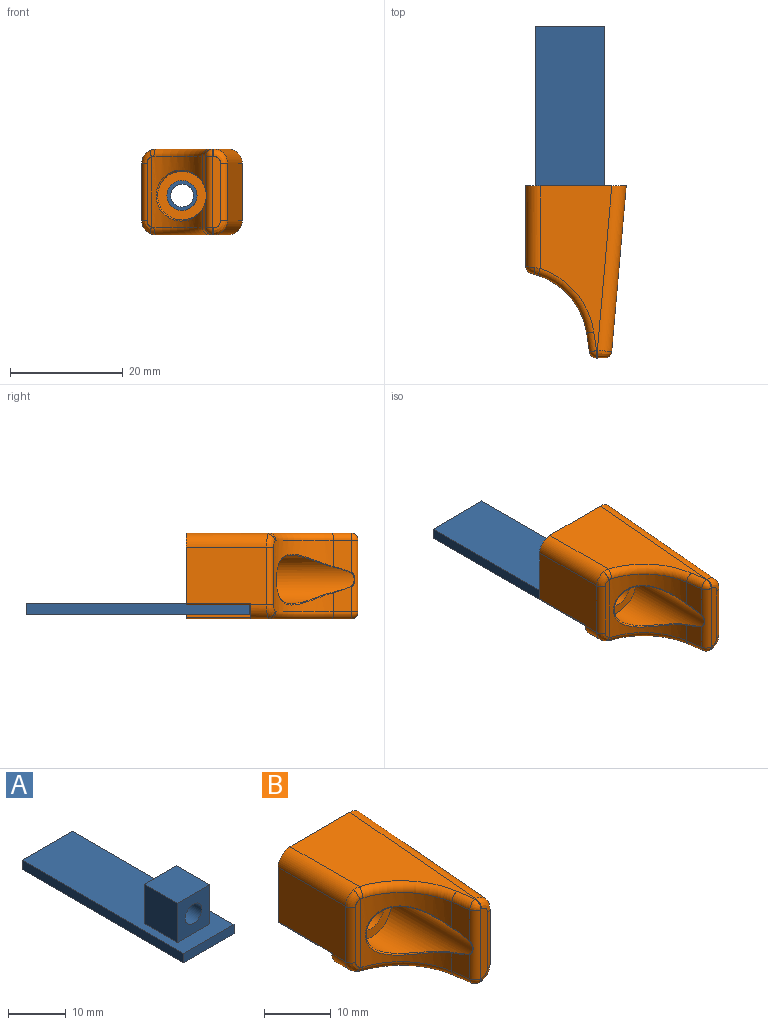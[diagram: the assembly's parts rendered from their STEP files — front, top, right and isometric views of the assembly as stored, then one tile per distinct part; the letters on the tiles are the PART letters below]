
ASSEMBLY  parts=2 mates=1
PART A: 12 faces, bbox 12.3x39.6x10.3 mm
  f0: plane 39.62x12.27mm, normal (0,0,1), area 421.8mm2, adj f1,f2,f3,f4,f6,f7,f8,f9
  f1: plane 39.62x1.96mm, normal (-1,0,0), area 77.5mm2, adj f0,f2,f4,f5
  f2: plane 12.27x1.96mm, normal (0,-1,0), area 24mm2, adj f0,f1,f3,f5
  f3: plane 39.62x1.96mm, normal (1,0,0), area 77.5mm2, adj f0,f2,f4,f5
  f4: plane 12.27x1.96mm, normal (0,1,0), area 24mm2, adj f0,f1,f3,f5
  f5: plane 39.62x12.27mm, normal (0,0,-1), area 486mm2, adj f1,f2,f3,f4
  f6: plane 8.31x8.13mm, normal (-1,0,0), area 67.5mm2, adj f0,f7,f9,f10
  f7: plane 8.31x7.9mm, normal (0,-1,0), area 52.6mm2, adj f0,f6,f8,f10,f11
  f8: plane 8.31x8.13mm, normal (1,0,0), area 67.5mm2, adj f0,f7,f9,f10
  f9: plane 8.31x7.9mm, normal (0,1,0), area 52.6mm2, adj f0,f6,f8,f10,f11
  f10: plane 8.13x7.9mm, normal (0,0,1), area 64.2mm2, adj f6,f7,f8,f9
  f11: cylinder r=2.03mm len=8.13mm, axis (0,-1,0), area 103.8mm2, adj f7,f9
PART B: 50 faces, bbox 17.9x30.8x15.4 mm
  f0: plane 9.22x0.81mm, normal (0,0,-1), area 3.7mm2, adj f9,f22,f48
  f1: plane 12.7x1.42mm, normal (0,-1,0), area 17.4mm2, adj f28,f29,f32,f35,f36,f38
  f2: plane 29.21x12.69mm, normal (0,0,1), area 226.8mm2, adj f9,f23,f24,f38,f39,f41
  f3: cylinder r=4.32mm len=17.09mm, axis (0,-1,0), area 208.3mm2, adj f16,f42,f43,f44,f45
  f4: cylinder r=2.67mm len=5.33mm, axis (0,1,0), area 76.6mm2, adj f15,f16
  f5: plane 14.02x11.43mm, normal (0,0,-1), area 91mm2, adj f9,f10,f11,f15,f46,f47,f49
  f6: plane 14.28x10.16mm, normal (-1,0,0), area 142.8mm2, adj f9,f11,f21,f24,f31,f49
  f7: plane 17.78x11.69mm, normal (0,0,-1), area 87.4mm2, adj f11,f21,f22,f26,f29,f30
  f8: plane 29.32x10.16mm, normal (1,-0.09,0), area 299mm2, adj f9,f22,f23,f32
  f9: plane 17.87x15.33mm, normal (0,1,0), area 158.4mm2, adj f0,f2,f5,f6,f8,f10,f12,f13
  f10: plane 11.43x2.34mm, normal (-1,0,0), area 26.7mm2, adj f5,f9,f11,f48
  f11: plane 14.38x2.74mm, normal (0,1,0), area 34.8mm2, adj f5,f6,f7,f10,f21,f22,f48,f49
  f12: plane 8.69x8.13mm, normal (-1,0,0), area 70.6mm2, adj f9,f14,f15,f46
  f13: plane 8.69x8.13mm, normal (1,0,0), area 70.6mm2, adj f9,f14,f15,f47
  f14: plane 8.13x8.13mm, normal (0,0,-1), area 66.1mm2, adj f9,f12,f13,f15
  f15: plane 8.89x8.53mm, normal (0,1,0), area 49.9mm2, adj f4,f5,f12,f13,f14,f46,f47
  f16: plane 8.64x8.64mm, normal (0,-1,0), area 36.2mm2, adj f3,f4
  f17: plane 4.52x3.3mm, normal (-0.99,-0.15,0), area 12.9mm2, adj f19,f30,f36,f43
  f18: plane 5.79x3.3mm, normal (-0.99,-0.15,0), area 17.2mm2, adj f19,f36,f41,f44
  f19: cylinder r=12.7mm len=12.7mm, axis (0,0,-1), area 85.9mm2, adj f17,f18,f20,f25,f26,f37,f39,f42
  f20: plane 12.51x0.79mm, normal (-0.27,-0.96,0), area 9.7mm2, adj f19,f27,f31,f34
  f21: cylinder r=2.54mm len=3.22mm, axis (0,-1,0), area 12mm2, adj f6,f7,f11,f25,f27
  f22: cylinder r=2.54mm len=29.65mm, axis (-0.09,-1,0), area 117mm2, adj f0,f7,f8,f9,f11,f28,f48
  f23: cylinder r=2.54mm len=29.65mm, axis (0.09,1,0), area 117.2mm2, adj f2,f8,f9,f35
  f24: cylinder r=2.54mm len=14.65mm, axis (0,1,0), area 57.6mm2, adj f2,f6,f9,f34,f37
  f25: bspline ~2.25x1.61mm, area 1.5mm2, adj f19,f21,f26,f27
  f26: torus R=13.97mm, axis (0,0,1), area 29.2mm2, adj f7,f19,f25,f30
  f27: bspline ~2.35x1.71mm, area 4.1mm2, adj f20,f21,f25,f31
  f28: bspline ~2.54x2.54mm, area 6.2mm2, adj f1,f22,f29,f32
  f29: cylinder r=1.27mm len=1.27mm, axis (-1,0,0), area 0.3mm2, adj f1,f7,f28,f33
  f30: cylinder r=1.27mm len=3.48mm, axis (0.15,-0.99,0), area 6.6mm2, adj f7,f17,f26,f33
  f31: cylinder r=1.27mm len=10.16mm, axis (0,0,1), area 16.7mm2, adj f6,f20,f27,f34
  f32: cylinder r=1.27mm len=10.16mm, axis (0,0,1), area 19.1mm2, adj f1,f8,f28,f35
  f33: sphere r=1.27mm, area 2.3mm2, adj f29,f30,f36
  f34: bspline ~2.35x1.71mm, area 4.1mm2, adj f20,f24,f31,f37
  f35: bspline ~2.54x2.54mm, area 6.2mm2, adj f1,f23,f32,f38
  f36: cylinder r=1.27mm len=12.7mm, axis (0,0,-1), area 22mm2, adj f1,f17,f18,f33,f40,f45
  f37: bspline ~2.25x1.61mm, area 1.5mm2, adj f19,f24,f34,f39
  f38: cylinder r=1.27mm len=1.27mm, axis (1,0,0), area 0.3mm2, adj f1,f2,f35,f40
  f39: torus R=13.97mm, axis (0,0,1), area 29.2mm2, adj f2,f19,f37,f41
  f40: sphere r=1.27mm, area 2.3mm2, adj f36,f38,f41
  f41: cylinder r=1.27mm len=3.48mm, axis (0.15,-0.99,0), area 6.6mm2, adj f2,f18,f39,f40
  f42: bspline ~11.03x9.05mm, area 9.2mm2, adj f3,f19,f43,f44
  f43: bspline ~3.33x1.18mm, area 0.3mm2, adj f3,f17,f42,f45
  f44: bspline ~3.33x1.18mm, area 0.3mm2, adj f3,f18,f42,f45
  f45: bspline ~2.43x0.6mm, area 0.3mm2, adj f3,f36,f43,f44
  f46: cylinder r=0.2mm len=8.13mm, axis (0,1,0), area 2.6mm2, adj f5,f9,f12,f15
  f47: cylinder r=0.2mm len=8.13mm, axis (0,-1,0), area 2.6mm2, adj f5,f9,f13,f15
  f48: cylinder r=0.2mm len=11.43mm, axis (0,-1,0), area 3.5mm2, adj f0,f9,f10,f11,f22
  f49: cylinder r=0.2mm len=11.43mm, axis (0,1,0), area 3.6mm2, adj f5,f6,f9,f11
PLACE A t=(0.21,-9.2,-2.89)mm
PLACE B t=(13.98,-3.75,4.77)mm
MATE cylindrical A.f11 <-> B.f3  axis (0,-1,0) through (-1.29,-11.88,3.22)mm
